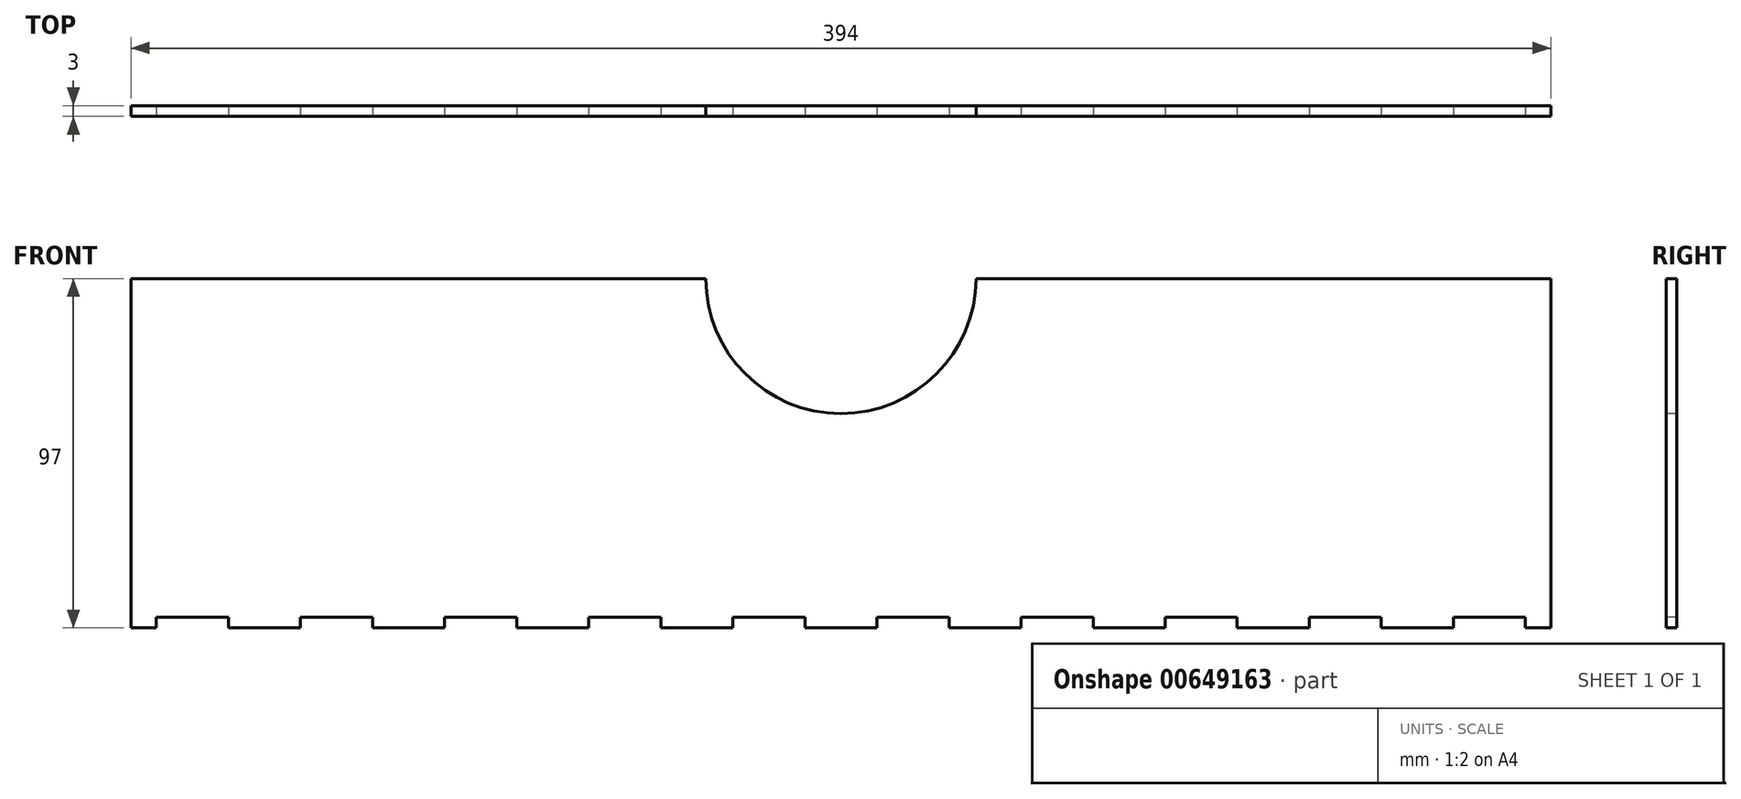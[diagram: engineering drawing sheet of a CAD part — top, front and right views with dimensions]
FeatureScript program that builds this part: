
annotation { "Feature Type Name" : "Feature", "Feature Type Description" : "" }
export const myFeature = defineFeature(function(context is Context, id is Id, definition is map)
    precondition{}
    {
        {
            var Q0;
            Q0=qCreatedBy(makeId("Front.planeOp"),FACE);
            var sketch = newSketch(context, id + "F0", { "sketchPlane" : qUnion([Q0])});
            skLineSegment(sketch, "E0.bottom", {"start": v(197, 47) * mm, "end": v(-197, 47) * mm});
            skLineSegment(sketch, "E0.top", {"start": v(197, -47) * mm, "end": v(-197, -47) * mm});
            skLineSegment(sketch, "E0.left", {"start": v(197, 47) * mm, "end": v(197, -47) * mm});
            skLineSegment(sketch, "E0.right", {"start": v(-197, 47) * mm, "end": v(-197, -47) * mm});
            skPoint(sketch, "E0.middle", {"position": v(0, 0) * mm});
            skSolve(sketch);
        }
        {
            var Q0;
            Q0=makeQuery(id+"F0.imprint","IMPRINT",FACE,{"disambiguationData":[TD([[makeQuery(id+"F0.imprint","IMPRINT",EDGE,{"derivedFrom":sQuery(id+"F0.wireOp",EDGE,"E0.bottom")}),1.0]])]});
            extrude(context, id + "F1", {"entities" : qUnion([Q0]), "depth" : 3 * mm, "offsetDistance" : 25 * mm});
        }
        {
            var Q0;
            Q0=makeQuery(id+"F1.opExtrude","CAP_FACE",FACE,{"disambiguationData":[OSD([sQuery(id+"F0.wireOp",EDGE,"E0.bottom"),sQuery(id+"F0.wireOp",EDGE,"E0.top"),sQuery(id+"F0.wireOp",EDGE,"E0.left"),sQuery(id+"F0.wireOp",EDGE,"E0.right")])],"isStart":false});
            var sketch = newSketch(context, id + "F2", { "sketchPlane" : qUnion([Q0])});
            skLineSegment(sketch, "E1.bottom", {"start": v(-197, -47) * mm, "end": v(-190, -47) * mm});
            skLineSegment(sketch, "E1.top", {"start": v(-197, -50) * mm, "end": v(-190, -50) * mm});
            skLineSegment(sketch, "E1.left", {"start": v(-197, -47) * mm, "end": v(-197, -50) * mm});
            skLineSegment(sketch, "E1.right", {"start": v(-190, -47) * mm, "end": v(-190, -50) * mm});
            skLineSegment(sketch, "E2.bottom", {"start": v(197, -47) * mm, "end": v(190, -47) * mm});
            skLineSegment(sketch, "E2.top", {"start": v(197, -50) * mm, "end": v(190, -50) * mm});
            skLineSegment(sketch, "E2.left", {"start": v(197, -47) * mm, "end": v(197, -50) * mm});
            skLineSegment(sketch, "E2.right", {"start": v(190, -47) * mm, "end": v(190, -50) * mm});
            skLineSegment(sketch, "E3", {"start": v(-190, -47) * mm, "end": v(-170, -47) * mm, "construction": true});
            skLineSegment(sketch, "E4.bottom", {"start": v(-170, -47) * mm, "end": v(-150, -47) * mm});
            skLineSegment(sketch, "E4.top", {"start": v(-170, -50) * mm, "end": v(-150, -50) * mm});
            skLineSegment(sketch, "E4.left", {"start": v(-170, -47) * mm, "end": v(-170, -50) * mm});
            skLineSegment(sketch, "E4.right", {"start": v(-150, -47) * mm, "end": v(-150, -50) * mm});
            skLineSegment(sketch, "E5.1.0.0", {"start": v(-130, -47) * mm, "end": v(-110, -47) * mm});
            skLineSegment(sketch, "E5.1.0.1", {"start": v(-110, -47) * mm, "end": v(-110, -50) * mm});
            skLineSegment(sketch, "E5.1.0.2", {"start": v(-130, -50) * mm, "end": v(-110, -50) * mm});
            skLineSegment(sketch, "E5.1.0.3", {"start": v(-130, -47) * mm, "end": v(-130, -50) * mm});
            skLineSegment(sketch, "E5.2.0.0", {"start": v(-90, -47) * mm, "end": v(-70, -47) * mm});
            skLineSegment(sketch, "E5.2.0.1", {"start": v(-70, -47) * mm, "end": v(-70, -50) * mm});
            skLineSegment(sketch, "E5.2.0.2", {"start": v(-90, -50) * mm, "end": v(-70, -50) * mm});
            skLineSegment(sketch, "E5.2.0.3", {"start": v(-90, -47) * mm, "end": v(-90, -50) * mm});
            skLineSegment(sketch, "E5.3.0.0", {"start": v(-50, -47) * mm, "end": v(-30, -47) * mm});
            skLineSegment(sketch, "E5.3.0.1", {"start": v(-30, -47) * mm, "end": v(-30, -50) * mm});
            skLineSegment(sketch, "E5.3.0.2", {"start": v(-50, -50) * mm, "end": v(-30, -50) * mm});
            skLineSegment(sketch, "E5.3.0.3", {"start": v(-50, -47) * mm, "end": v(-50, -50) * mm});
            skLineSegment(sketch, "E5.4.0.0", {"start": v(-10, -47) * mm, "end": v(10, -47) * mm});
            skLineSegment(sketch, "E5.4.0.1", {"start": v(10, -47) * mm, "end": v(10, -50) * mm});
            skLineSegment(sketch, "E5.4.0.2", {"start": v(-10, -50) * mm, "end": v(10, -50) * mm});
            skLineSegment(sketch, "E5.4.0.3", {"start": v(-10, -47) * mm, "end": v(-10, -50) * mm});
            skLineSegment(sketch, "E5.5.0.0", {"start": v(30, -47) * mm, "end": v(50, -47) * mm});
            skLineSegment(sketch, "E5.5.0.1", {"start": v(50, -47) * mm, "end": v(50, -50) * mm});
            skLineSegment(sketch, "E5.5.0.2", {"start": v(30, -50) * mm, "end": v(50, -50) * mm});
            skLineSegment(sketch, "E5.5.0.3", {"start": v(30, -47) * mm, "end": v(30, -50) * mm});
            skLineSegment(sketch, "E5.6.0.0", {"start": v(70, -47) * mm, "end": v(90, -47) * mm});
            skLineSegment(sketch, "E5.6.0.1", {"start": v(90, -47) * mm, "end": v(90, -50) * mm});
            skLineSegment(sketch, "E5.6.0.2", {"start": v(70, -50) * mm, "end": v(90, -50) * mm});
            skLineSegment(sketch, "E5.6.0.3", {"start": v(70, -47) * mm, "end": v(70, -50) * mm});
            skLineSegment(sketch, "E5.7.0.0", {"start": v(110, -47) * mm, "end": v(130, -47) * mm});
            skLineSegment(sketch, "E5.7.0.1", {"start": v(130, -47) * mm, "end": v(130, -50) * mm});
            skLineSegment(sketch, "E5.7.0.2", {"start": v(110, -50) * mm, "end": v(130, -50) * mm});
            skLineSegment(sketch, "E5.7.0.3", {"start": v(110, -47) * mm, "end": v(110, -50) * mm});
            skLineSegment(sketch, "E5.8.0.0", {"start": v(150, -47) * mm, "end": v(170, -47) * mm});
            skLineSegment(sketch, "E5.8.0.1", {"start": v(170, -47) * mm, "end": v(170, -50) * mm});
            skLineSegment(sketch, "E5.8.0.2", {"start": v(150, -50) * mm, "end": v(170, -50) * mm});
            skLineSegment(sketch, "E5.8.0.3", {"start": v(150, -47) * mm, "end": v(150, -50) * mm});
            skLineSegment(sketch, "E5.direction1", {"start": v(-170, -50) * mm, "end": v(-130, -50) * mm, "construction": true});
            skSolve(sketch);
        }
        {
            var Q0;
            Q0 = qSketchRegion(id + "F2", true);
            var Q1;
            Q1=makeQuery(id+"F1.opExtrude","CAP_FACE",FACE,{"disambiguationData":[OSD([sQuery(id+"F0.wireOp",EDGE,"E0.bottom"),sQuery(id+"F0.wireOp",EDGE,"E0.top"),sQuery(id+"F0.wireOp",EDGE,"E0.left"),sQuery(id+"F0.wireOp",EDGE,"E0.right")])],"isStart":true});
            extrude(context, id + "F3", {"entities" : qUnion([Q0]), "operationType" : NewBodyOperationType.ADD, "endBound" : BoundingType.UP_TO_SURFACE, "oppositeDirection" : true, "depth" : 25 * mm, "endBoundEntityFace" : qUnion([Q1]), "offsetDistance" : 25 * mm});
        }
        {
            var Q0;
            Q0=makeQuery(id+"F3.boolean.opBoolean","MERGE",FACE,{"derivedFrom":[makeQuery(id+"F1.opExtrude","CAP_FACE",FACE,{"disambiguationData":[OSD([sQuery(id+"F0.wireOp",EDGE,"E0.bottom"),sQuery(id+"F0.wireOp",EDGE,"E0.top"),sQuery(id+"F0.wireOp",EDGE,"E0.left"),sQuery(id+"F0.wireOp",EDGE,"E0.right")])],"isStart":false}),makeQuery(id+"F3.opExtrude","CAP_FACE",FACE,{"disambiguationData":[OSD([sQuery(id+"F2.wireOp",EDGE,"E1.bottom"),sQuery(id+"F2.wireOp",EDGE,"E1.top"),sQuery(id+"F2.wireOp",EDGE,"E1.left"),sQuery(id+"F2.wireOp",EDGE,"E1.right")])],"isStart":true}),makeQuery(id+"F3.opExtrude","CAP_FACE",FACE,{"disambiguationData":[OSD([sQuery(id+"F2.wireOp",EDGE,"E2.bottom"),sQuery(id+"F2.wireOp",EDGE,"E2.top"),sQuery(id+"F2.wireOp",EDGE,"E2.left"),sQuery(id+"F2.wireOp",EDGE,"E2.right")])],"isStart":true}),makeQuery(id+"F3.opExtrude","CAP_FACE",FACE,{"disambiguationData":[OSD([sQuery(id+"F2.wireOp",EDGE,"E4.bottom"),sQuery(id+"F2.wireOp",EDGE,"E4.top"),sQuery(id+"F2.wireOp",EDGE,"E4.left"),sQuery(id+"F2.wireOp",EDGE,"E4.right")])],"isStart":true}),makeQuery(id+"F3.opExtrude","CAP_FACE",FACE,{"disambiguationData":[OSD([sQuery(id+"F2.wireOp",EDGE,"E5.1.0.0"),sQuery(id+"F2.wireOp",EDGE,"E5.1.0.1"),sQuery(id+"F2.wireOp",EDGE,"E5.1.0.2"),sQuery(id+"F2.wireOp",EDGE,"E5.1.0.3")])],"isStart":true}),makeQuery(id+"F3.opExtrude","CAP_FACE",FACE,{"disambiguationData":[OSD([sQuery(id+"F2.wireOp",EDGE,"E5.2.0.0"),sQuery(id+"F2.wireOp",EDGE,"E5.2.0.1"),sQuery(id+"F2.wireOp",EDGE,"E5.2.0.2"),sQuery(id+"F2.wireOp",EDGE,"E5.2.0.3")])],"isStart":true}),makeQuery(id+"F3.opExtrude","CAP_FACE",FACE,{"disambiguationData":[OSD([sQuery(id+"F2.wireOp",EDGE,"E5.3.0.0"),sQuery(id+"F2.wireOp",EDGE,"E5.3.0.1"),sQuery(id+"F2.wireOp",EDGE,"E5.3.0.2"),sQuery(id+"F2.wireOp",EDGE,"E5.3.0.3")])],"isStart":true}),makeQuery(id+"F3.opExtrude","CAP_FACE",FACE,{"disambiguationData":[OSD([sQuery(id+"F2.wireOp",EDGE,"E5.4.0.0"),sQuery(id+"F2.wireOp",EDGE,"E5.4.0.1"),sQuery(id+"F2.wireOp",EDGE,"E5.4.0.2"),sQuery(id+"F2.wireOp",EDGE,"E5.4.0.3")])],"isStart":true}),makeQuery(id+"F3.opExtrude","CAP_FACE",FACE,{"disambiguationData":[OSD([sQuery(id+"F2.wireOp",EDGE,"E5.5.0.0"),sQuery(id+"F2.wireOp",EDGE,"E5.5.0.1"),sQuery(id+"F2.wireOp",EDGE,"E5.5.0.2"),sQuery(id+"F2.wireOp",EDGE,"E5.5.0.3")])],"isStart":true}),makeQuery(id+"F3.opExtrude","CAP_FACE",FACE,{"disambiguationData":[OSD([sQuery(id+"F2.wireOp",EDGE,"E5.6.0.0"),sQuery(id+"F2.wireOp",EDGE,"E5.6.0.1"),sQuery(id+"F2.wireOp",EDGE,"E5.6.0.2"),sQuery(id+"F2.wireOp",EDGE,"E5.6.0.3")])],"isStart":true}),makeQuery(id+"F3.opExtrude","CAP_FACE",FACE,{"disambiguationData":[OSD([sQuery(id+"F2.wireOp",EDGE,"E5.7.0.0"),sQuery(id+"F2.wireOp",EDGE,"E5.7.0.1"),sQuery(id+"F2.wireOp",EDGE,"E5.7.0.2"),sQuery(id+"F2.wireOp",EDGE,"E5.7.0.3")])],"isStart":true}),makeQuery(id+"F3.opExtrude","CAP_FACE",FACE,{"disambiguationData":[OSD([sQuery(id+"F2.wireOp",EDGE,"E5.8.0.0"),sQuery(id+"F2.wireOp",EDGE,"E5.8.0.1"),sQuery(id+"F2.wireOp",EDGE,"E5.8.0.2"),sQuery(id+"F2.wireOp",EDGE,"E5.8.0.3")])],"isStart":true})]});
            var sketch = newSketch(context, id + "F4", { "sketchPlane" : qUnion([Q0])});
            skCircle(sketch, "E6", {"center": v(0, 47) * mm, "radius": 37.5 * mm});
            skSolve(sketch);
        }
        {
            var Q0;
            Q0 = qSketchRegion(id + "F4", true);
            extrude(context, id + "F5", {"entities" : qUnion([Q0]), "operationType" : NewBodyOperationType.REMOVE, "oppositeDirection" : true, "depth" : 25 * mm, "offsetDistance" : 25 * mm});
        }
    });
